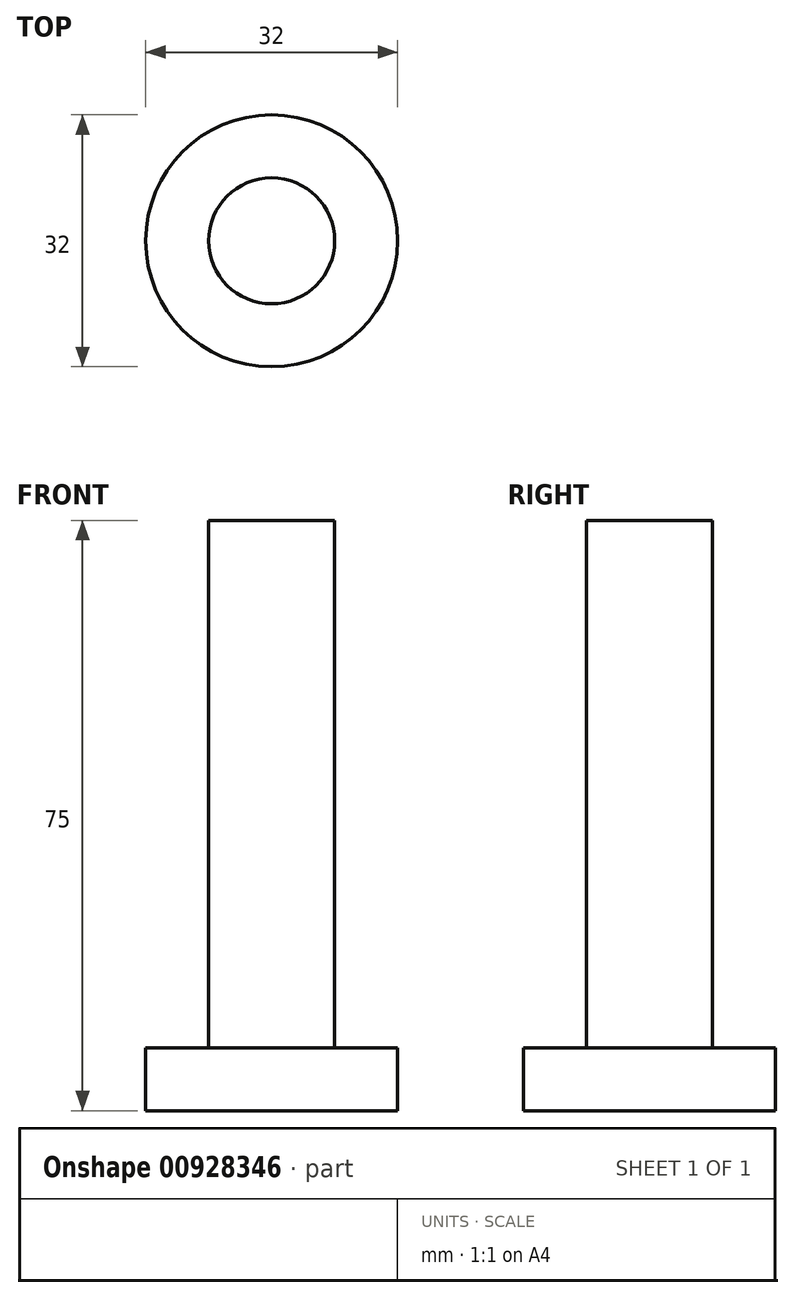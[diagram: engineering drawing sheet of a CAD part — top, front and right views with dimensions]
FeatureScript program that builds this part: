
annotation { "Feature Type Name" : "Feature", "Feature Type Description" : "" }
export const myFeature = defineFeature(function(context is Context, id is Id, definition is map)
    precondition{}
    {
        {
            var Q0;
            Q0=qCreatedBy(makeId("Front.planeOp"),FACE);
            var sketch = newSketch(context, id + "F0", { "sketchPlane" : qUnion([Q0])});
            skLineSegment(sketch, "E0", {"start": v(16, 0) * mm, "end": v(16, 8) * mm});
            skLineSegment(sketch, "E1", {"start": v(16, 8) * mm, "end": v(8, 8) * mm});
            skLineSegment(sketch, "E2", {"start": v(8, 8) * mm, "end": v(8, 75) * mm});
            skLineSegment(sketch, "E3", {"start": v(8, 75) * mm, "end": v(0, 75) * mm});
            skLineSegment(sketch, "E4", {"start": v(0, 0) * mm, "end": v(16, 0) * mm});
            skLineSegment(sketch, "E5", {"start": v(0, 0) * mm, "end": v(0, 75) * mm});
            skSolve(sketch);
        }
        {
            var Q0;
            Q0=makeQuery(id+"F0.imprint","IMPRINT",FACE,{"disambiguationData":[TD([[makeQuery(id+"F0.imprint","IMPRINT",EDGE,{"derivedFrom":sQuery(id+"F0.wireOp",EDGE,"E0")}),1.0]])]});
            var Q1;
            Q1=sQuery(id+"F0.wireOp",EDGE,"E5");
            revolve(context, id + "F1", {"surfaceOperationType" : NewSurfaceOperationType.NEW, "entities" : qUnion([Q0]), "axis" : qUnion([Q1]), "revolveType" : RevolveType.FULL});
        }
    });
